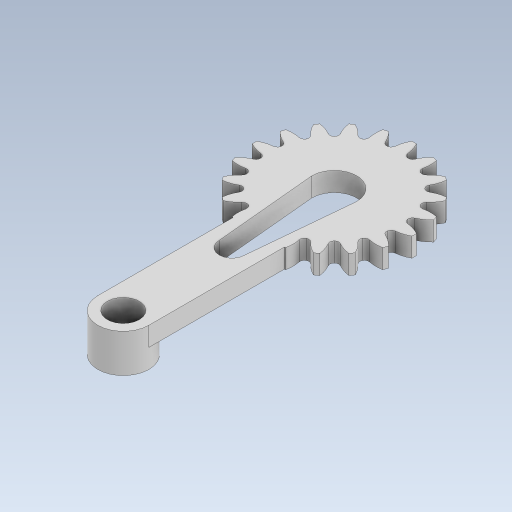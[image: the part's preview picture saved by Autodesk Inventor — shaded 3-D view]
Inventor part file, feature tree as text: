
AUTODESK INVENTOR PART (.ipt)
format: ipt  version: 2023.5 (Build 275446000, 446)  size: 521,728 bytes
history: native  units: in
note: dims shown in document units (in); Inventor stores cm internally (conversion verified against a paired STEP export)
features: extrude x5, sketch x3, fillet x1, pattern_circular x1, plane x1
ambient origin geometry x8: Origin, YZ Plane, XZ Plane, XY Plane, X Axis, Y Axis, Z Axis, Center Point
bodies: Solid1 (feature_tree)
feature tree (11):
  sketch  "Sketch1"  dims[d0=0.7874in d1=0.9843in]
  extrude  "Extrusion1"  Depth=0.9843in
  extrude  "Extrusion3"  Depth=0.0787in
  fillet  "Fillet1"  Radius=0.0276in
  pattern_circular  "Circular Pattern1"  [2 undecoded]
  plane  "Work Plane1"
  sketch  "Sketch2"  dims[d2=0.9055in d3=0.0787in d4=0.0276in]
  extrude  "Extrusion4"  Depth=0.0276in
  extrude  "Extrusion5"  Depth=0.1181in TaperAngle=360.0deg
  extrude  "Extrusion6"  Depth=0.1181in
  sketch  "Sketch3"  dims[d5=0.1181in d6=0.0in d9=0.1181in d10=0.0in d11=0.0276in d12=7.874in d13=360.0deg d15=0.1969in d16=0.315in d17=1.2992in d18=0.2756in d19=0.1969in d20=0.1181in d21=0.0in d22=0.1772in d23=0.0in d24=0.2756in d25=0.1575in d26=0.6299in d27=0.2756in d28=0.1575in d29=0.6299in d30=0.1181in d31=0.0in]
note: 2 required parameter values undecoded (feature->parameter linkage not recoverable at this tier; creation-order binding heuristic only, values carry confidence <= 0.55)
